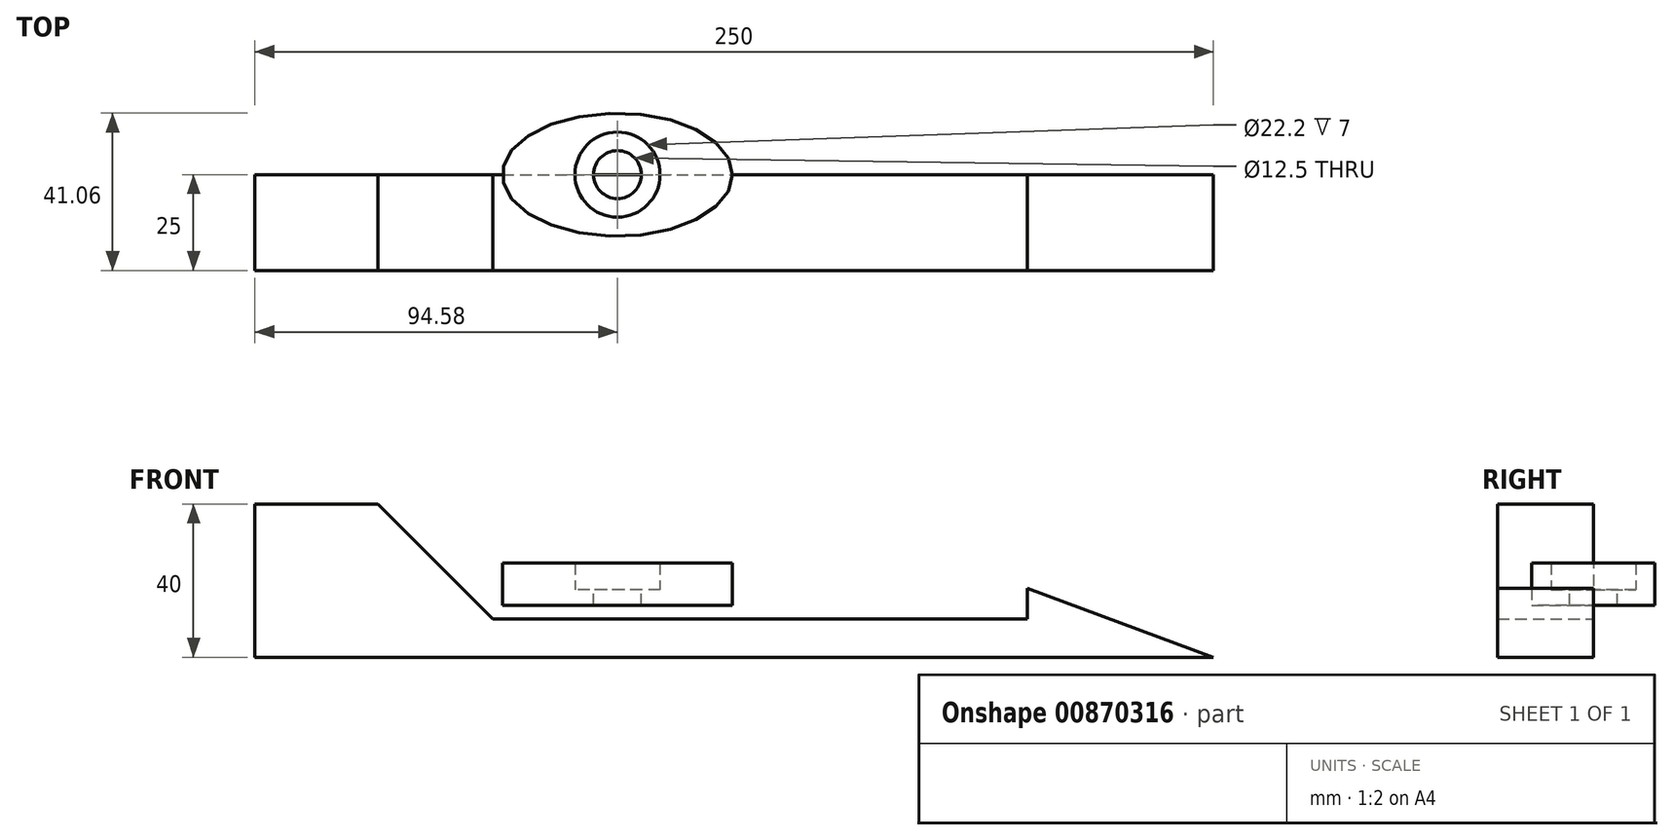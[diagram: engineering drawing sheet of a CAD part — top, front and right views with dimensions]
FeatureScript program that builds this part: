
annotation { "Feature Type Name" : "Feature", "Feature Type Description" : "" }
export const myFeature = defineFeature(function(context is Context, id is Id, definition is map)
    precondition{}
    {
        {
            var Q0;
            Q0=qCreatedBy(makeId("Top.planeOp"),FACE);
            var sketch = newSketch(context, id + "F0", { "sketchPlane" : qUnion([Q0])});
            skCircle(sketch, "E0", {"center": v(0, 0) * mm, "radius": 11.1 * mm});
            skEllipse(sketch, "E1", {"center": v(0, 0) * mm, "majorRadius": 30 * mm, "minorRadius": 16.06 * mm, "majorAxis": v(1, 0)});
            skCircle(sketch, "E2", {"center": v(0, 0) * mm, "radius": 6.25 * mm});
            skSolve(sketch);
        }
        {
            var Q0;
            Q0=makeQuery(id+"F0.imprint","IMPRINT",FACE,{"disambiguationData":[TD([[makeQuery(id+"F0.imprint","IMPRINT",EDGE,{"derivedFrom":sQuery(id+"F0.wireOp",EDGE,"E0")}),-1.0]])]});
            extrude(context, id + "F1", {"entities" : qUnion([Q0]), "depth" : 7 * mm, "offsetDistance" : 25 * mm});
        }
        {
            var Q0;
            Q0=makeQuery(id+"F0.imprint","IMPRINT",FACE,{"disambiguationData":[TD([[makeQuery(id+"F0.imprint","IMPRINT",EDGE,{"derivedFrom":sQuery(id+"F0.wireOp",EDGE,"E0")}),1.0]])]});
            var Q1;
            Q1=makeQuery(id+"F0.imprint","IMPRINT",FACE,{"disambiguationData":[TD([[makeQuery(id+"F0.imprint","IMPRINT",EDGE,{"derivedFrom":sQuery(id+"F0.wireOp",EDGE,"E0")}),-1.0]])]});
            extrude(context, id + "F2", {"entities" : qUnion([Q0, Q1]), "operationType" : NewBodyOperationType.ADD, "oppositeDirection" : true, "depth" : 4 * mm, "offsetDistance" : 25 * mm});
        }
        {
            var Q0;
            Q0=qCreatedBy(makeId("Front.planeOp"),FACE);
            var sketch = newSketch(context, id + "F3", { "sketchPlane" : qUnion([Q0])});
            skLineSegment(sketch, "E3", {"start": v(-32.53, -7.59) * mm, "end": v(106.88, -7.59) * mm});
            skLineSegment(sketch, "E4", {"start": v(-32.53, -7.59) * mm, "end": v(-62.45, 22.41) * mm});
            skLineSegment(sketch, "E5", {"start": v(-62.45, 22.41) * mm, "end": v(-94.58, 22.41) * mm});
            skLineSegment(sketch, "E6", {"start": v(-94.58, 22.41) * mm, "end": v(-94.58, -17.59) * mm});
            skLineSegment(sketch, "E7", {"start": v(-94.58, -17.59) * mm, "end": v(155.42, -17.59) * mm});
            skLineSegment(sketch, "E8", {"start": v(106.88, 0.41) * mm, "end": v(155.42, -17.59) * mm});
            skLineSegment(sketch, "E9", {"start": v(106.88, 0.41) * mm, "end": v(106.88, -7.59) * mm});
            skSolve(sketch);
        }
        {
            var Q0;
            Q0=makeQuery(id+"F3.imprint","IMPRINT",FACE,{"disambiguationData":[TD([[makeQuery(id+"F3.imprint","IMPRINT",EDGE,{"derivedFrom":sQuery(id+"F3.wireOp",EDGE,"E3")}),-1.0]])]});
            extrude(context, id + "F4", {"entities" : qUnion([Q0]), "depth" : 25 * mm, "offsetDistance" : 25 * mm});
        }
    });
